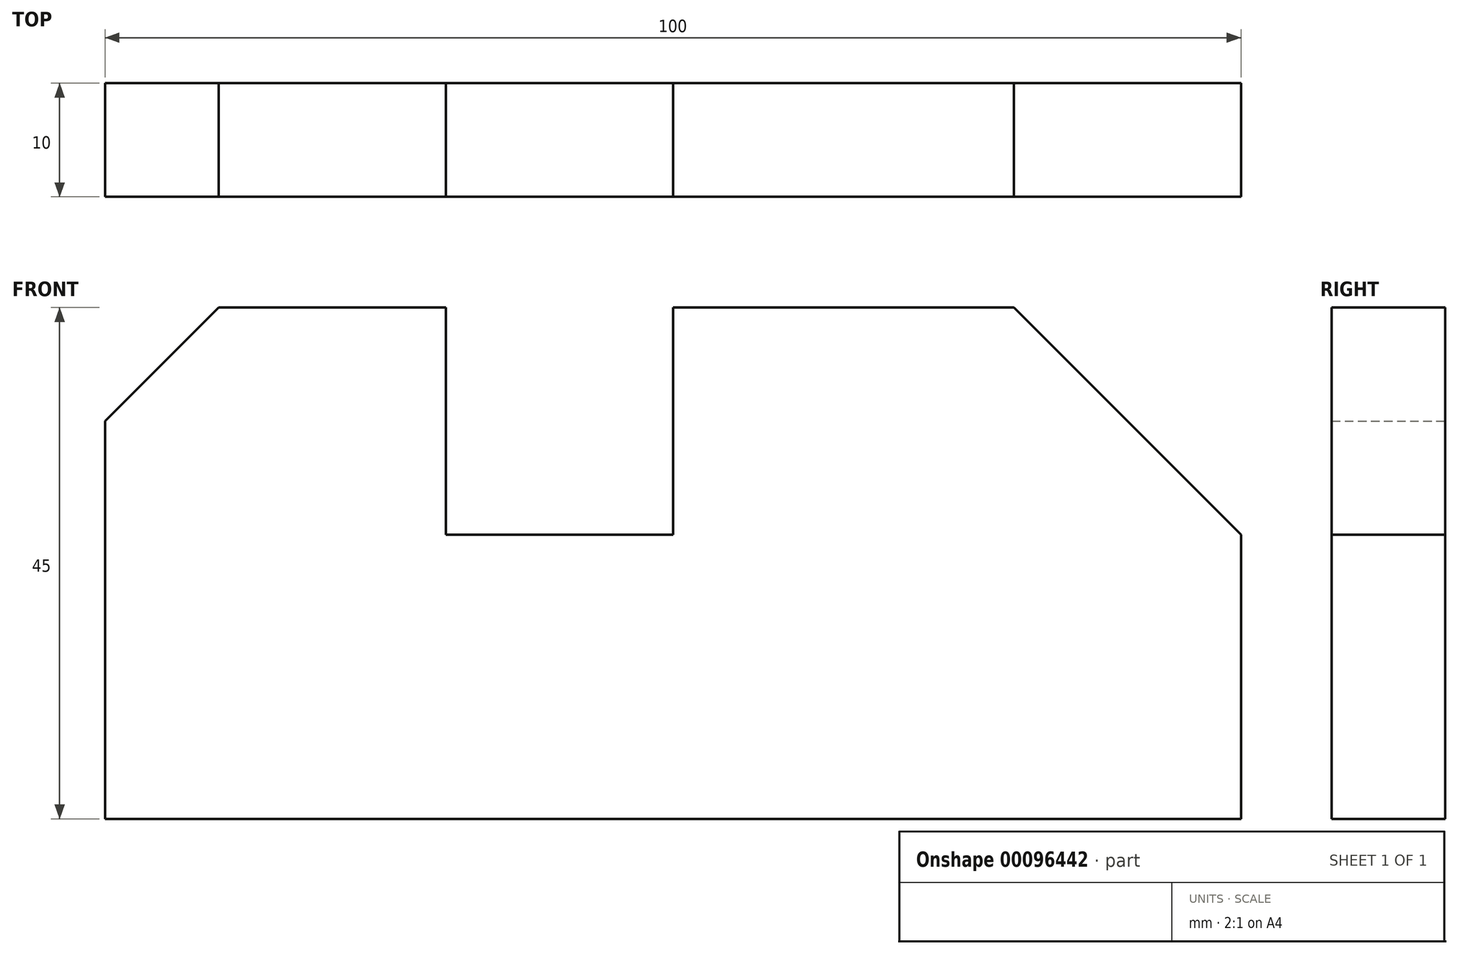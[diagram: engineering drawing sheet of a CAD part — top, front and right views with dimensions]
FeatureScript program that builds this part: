
annotation { "Feature Type Name" : "Feature", "Feature Type Description" : "" }
export const myFeature = defineFeature(function(context is Context, id is Id, definition is map)
    precondition{}
    {
        {
            var Q0;
            Q0=qCreatedBy(makeId("Front.planeOp"),FACE);
            var sketch = newSketch(context, id + "F0", { "sketchPlane" : qUnion([Q0])});
            skLineSegment(sketch, "E0", {"start": v(0, 0) * mm, "end": v(0, 35) * mm});
            skLineSegment(sketch, "E1", {"start": v(0, 35) * mm, "end": v(10, 45) * mm});
            skLineSegment(sketch, "E2", {"start": v(10, 45) * mm, "end": v(30, 45) * mm});
            skLineSegment(sketch, "E3", {"start": v(30, 45) * mm, "end": v(30, 25) * mm});
            skLineSegment(sketch, "E4", {"start": v(30, 25) * mm, "end": v(50, 25) * mm});
            skLineSegment(sketch, "E5", {"start": v(50, 25) * mm, "end": v(50, 45) * mm});
            skLineSegment(sketch, "E6", {"start": v(50, 45) * mm, "end": v(80, 45) * mm});
            skLineSegment(sketch, "E7", {"start": v(80, 45) * mm, "end": v(100, 25) * mm});
            skLineSegment(sketch, "E8", {"start": v(100, 25) * mm, "end": v(100, 0) * mm});
            skLineSegment(sketch, "E9", {"start": v(100, 0) * mm, "end": v(0, 0) * mm});
            skLineSegment(sketch, "E10", {"start": v(30, 45) * mm, "end": v(128.54, 45) * mm, "construction": true});
            skSolve(sketch);
        }
        {
            var Q0;
            Q0 = qSketchRegion(id + "F0", true);
            extrude(context, id + "F1", {"entities" : qUnion([Q0]), "depth" : 10 * mm});
        }
    });
